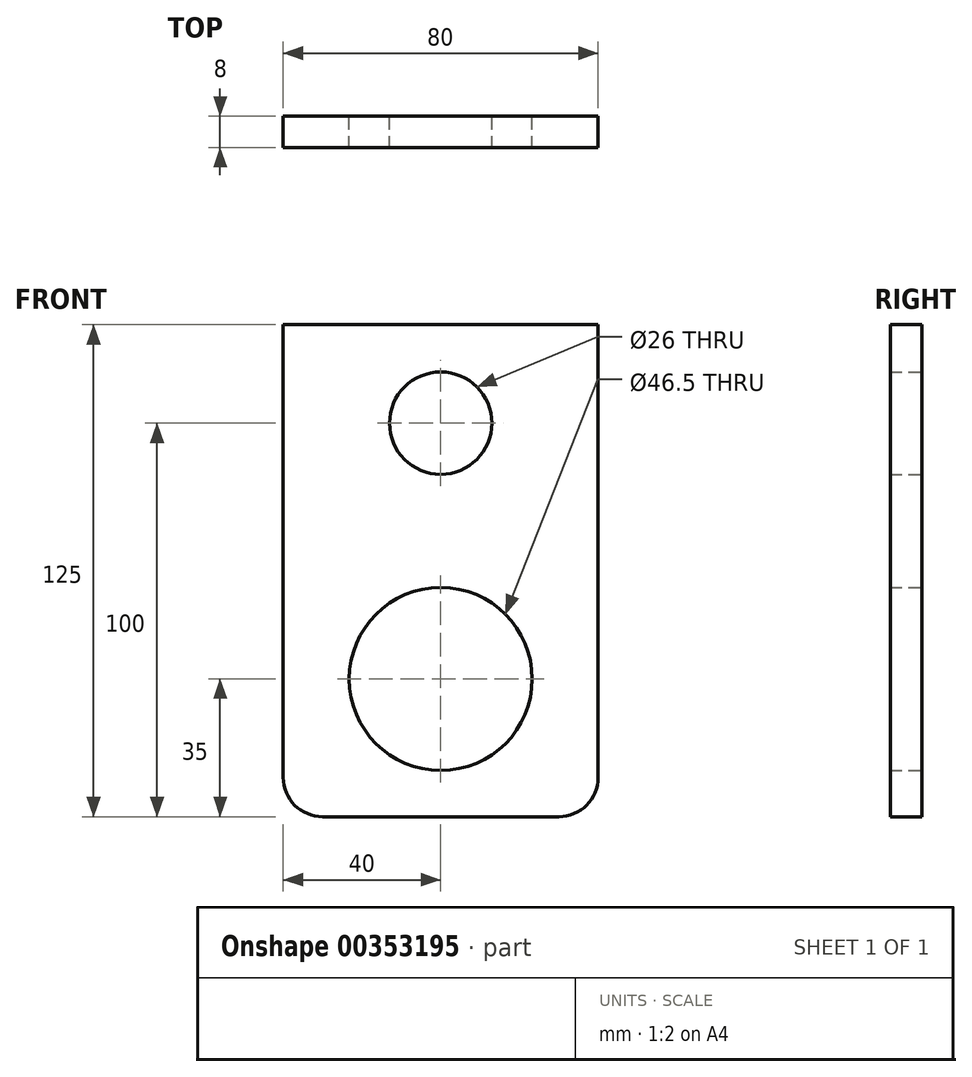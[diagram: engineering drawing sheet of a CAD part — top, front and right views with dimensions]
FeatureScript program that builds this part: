
annotation { "Feature Type Name" : "Feature", "Feature Type Description" : "" }
export const myFeature = defineFeature(function(context is Context, id is Id, definition is map)
    precondition{}
    {
        {
            var Q0;
            Q0=qCreatedBy(makeId("Front.planeOp"),FACE);
            var sketch = newSketch(context, id + "F0", { "sketchPlane" : qUnion([Q0])});
            skLineSegment(sketch, "E0.bottom", {"start": v(40, 62.5) * mm, "end": v(-40, 62.5) * mm});
            skLineSegment(sketch, "E0.top", {"start": v(30, -62.5) * mm, "end": v(-30, -62.5) * mm});
            skLineSegment(sketch, "E0.left", {"start": v(40, 62.5) * mm, "end": v(40, -52.5) * mm});
            skLineSegment(sketch, "E0.right", {"start": v(-40, 62.5) * mm, "end": v(-40, -52.5) * mm});
            skPoint(sketch, "E0.middle", {"position": v(0, 0) * mm});
            skCircle(sketch, "E1", {"center": v(0, 37.5) * mm, "radius": 13 * mm});
            skCircle(sketch, "E2", {"center": v(0, -27.5) * mm, "radius": 23.25 * mm});
            skLineSegment(sketch, "E3", {"start": v(0, 37.5) * mm, "end": v(49, 37.5) * mm, "construction": true});
            skLineSegment(sketch, "E4", {"start": v(0, -27.5) * mm, "end": v(65.11, -27.5) * mm, "construction": true});
            skPoint(sketch, "E5.visualSharp", {"position": v(-40, -62.5) * mm});
            skArc(sketch, "E5.filletArc", {"start": v(-40, -52.5) * mm, "mid": v(-37.07, -59.57) * mm, "end": v(-30, -62.5) * mm});
            skPoint(sketch, "E6.visualSharp", {"position": v(40, -62.5) * mm});
            skArc(sketch, "E6.filletArc", {"start": v(30, -62.5) * mm, "mid": v(37.07, -59.57) * mm, "end": v(40, -52.5) * mm});
            skSolve(sketch);
        }
        {
            var Q0;
            Q0=makeQuery(id+"F0.imprint","IMPRINT",FACE,{"disambiguationData":[TD([[makeQuery(id+"F0.imprint","IMPRINT",EDGE,{"derivedFrom":sQuery(id+"F0.wireOp",EDGE,"E0.bottom")}),1.0]])]});
            extrude(context, id + "F1", {"entities" : qUnion([Q0]), "depth" : 8 * mm});
        }
    });
